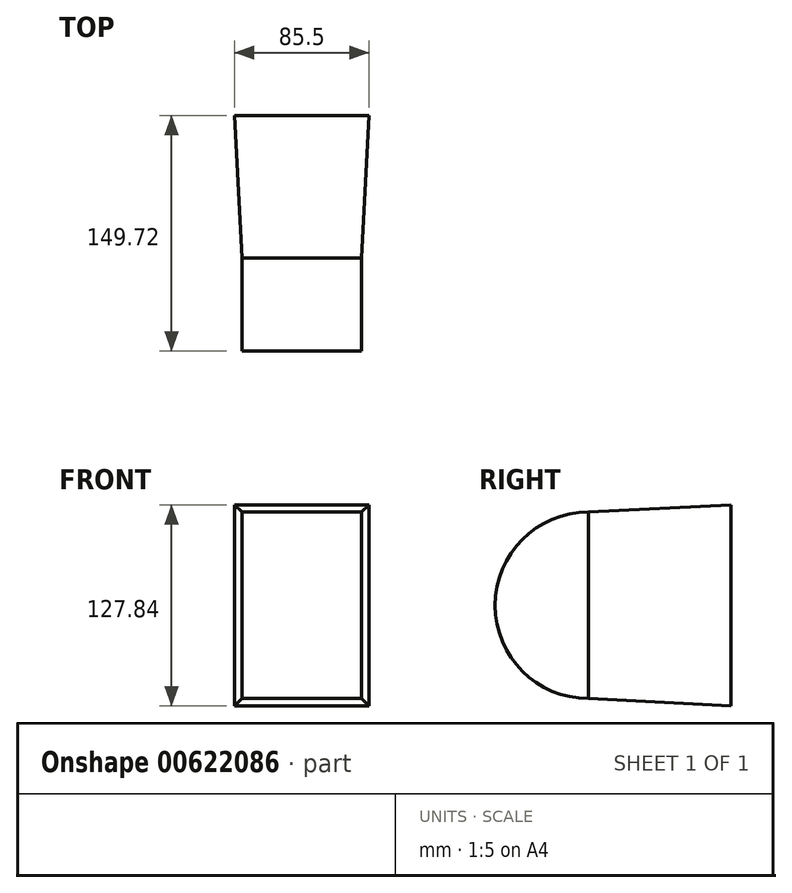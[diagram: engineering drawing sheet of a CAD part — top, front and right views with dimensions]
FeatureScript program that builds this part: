
annotation { "Feature Type Name" : "Feature", "Feature Type Description" : "" }
export const myFeature = defineFeature(function(context is Context, id is Id, definition is map)
    precondition{}
    {
        {
            var Q0;
            Q0=qCreatedBy(makeId("Front.planeOp"),FACE);
            var sketch = newSketch(context, id + "F0", { "sketchPlane" : qUnion([Q0])});
            skLineSegment(sketch, "E0.bottom", {"start": v(38, -29.59) * mm, "end": v(-38, -29.59) * mm});
            skLineSegment(sketch, "E0.top", {"start": v(38, 29.59) * mm, "end": v(-38, 29.59) * mm});
            skLineSegment(sketch, "E0.left", {"start": v(38, -29.59) * mm, "end": v(38, 29.59) * mm});
            skLineSegment(sketch, "E0.right", {"start": v(-38, -29.59) * mm, "end": v(-38, 29.59) * mm});
            skPoint(sketch, "E0.middle", {"position": v(0, 0) * mm});
            skSolve(sketch);
        }
        {
            var Q0;
            Q0=makeQuery(id+"F0.imprint","IMPRINT",FACE,{"disambiguationData":[TD([[makeQuery(id+"F0.imprint","IMPRINT",EDGE,{"derivedFrom":sQuery(id+"F0.wireOp",EDGE,"E0.bottom")}),-1.0]])]});
            var Q1;
            Q1=sQuery(id+"F0.wireOp",EDGE,"E0.top");
            revolve(context, id + "F1", {"entities" : qUnion([Q0]), "axis" : qUnion([Q1]), "revolveType" : RevolveType.ONE_DIRECTION, "angle" : 180 * degree});
        }
        {
            var Q0;
            Q0=makeQuery(id+"F1.opRevolve","CAP_FACE",FACE,{"disambiguationData":[OSD([sQuery(id+"F0.wireOp",EDGE,"E0.bottom"),sQuery(id+"F0.wireOp",EDGE,"E0.top"),sQuery(id+"F0.wireOp",EDGE,"E0.left"),sQuery(id+"F0.wireOp",EDGE,"E0.right")])],"isStart":true});
            extrude(context, id + "F2", {"entities" : qUnion([Q0]), "operationType" : NewBodyOperationType.ADD, "depth" : 90.55 * mm, "offsetDistance" : 25.4 * mm, "hasDraft" : true, "draftAngle" : 3 * degree});
        }
    });
